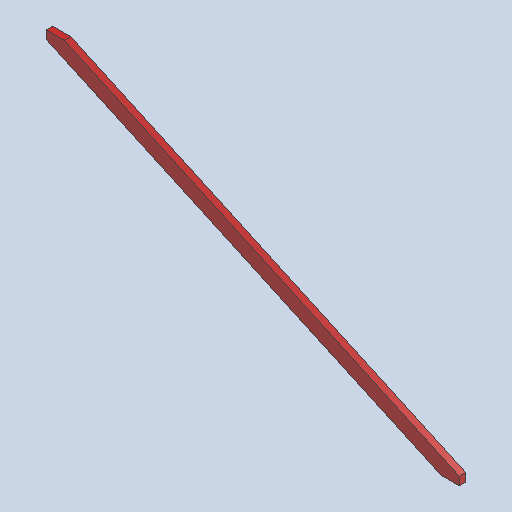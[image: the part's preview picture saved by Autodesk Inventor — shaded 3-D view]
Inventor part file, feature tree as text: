
AUTODESK INVENTOR PART (.ipt)
format: ipt  version: 2025.1 (Build 291241020, 241B)  size: 256,512 bytes
history: native  units: in
note: dims shown in document units (in); Inventor stores cm internally (conversion verified against a paired STEP export)
features: other x7, reference x5, extrude x1, sketch x1
ambient origin geometry x8: Origin, YZ Plane, XZ Plane, XY Plane, X Axis, Y Axis, Z Axis, Center Point
bodies: Solid1 (feature_tree)
feature tree (14):
  extrude  "Extrusion1"  [1 undecoded]
  sketch  "Sketch1"  dims[d2=1.5in d3=0.0in]
  reference  "Reference1"
  reference  "Reference2"
  reference  "Reference3"
  reference  "Reference4"
  reference  "Reference5"
  other  "<userpath>\Documents\Tburn24\layer1\layer1.iam"
  other  "layer1.iam"
  other  "10'x2x4:9"
  other  "7'5x2x4:1"
  other  "7'5x2x4:8"
  other  "10'x2x4:2"
  other  "Finish1"
note: 1 required parameter value undecoded (feature->parameter linkage not recoverable at this tier; creation-order binding heuristic only, values carry confidence <= 0.55)
